FCSTD DOCUMENT  (FreeCAD 1.0R39109 (Git))
Label: Pistol
License: All rights reserved
LicenseURL: http://en.wikipedia.org/wiki/All_rights_reserved
objects: App::Link×6, Image::ImagePlane×1, App::Part×1
EXTERNAL_REF file=Parts/SizeRequirements.FCStd obj=Part
EXTERNAL_REF file=../../Reference/Pardini-SP22.FCStd obj=Part
EXTERNAL_REF file=Parts/Handgrip.stl.FCStd obj=Part
EXTERNAL_REF file=Parts/FrameAssembly.FCStd obj=Part
EXTERNAL_REF file=Parts/SidePlateRight.stl.FCStd obj=Part001
EXTERNAL_REF file=Parts/SidePlateLeft.stl.FCStd obj=Part

FEATURE [App::Link] Link  label="SizeRequirements"
  LinkPlacement = pos=(19.75,13.25,0) rot=(0,0,1;0rad)
  LinkedObject = -> <external Parts/SizeRequirements.FCStd>#Part
  Placement = pos=(19.75,13.25,0) rot=(0,0,1;0rad)
FEATURE [Image::ImagePlane] ecoaims_pp320expt  label="ecoaims-pp320expt"
  Placement = pos=(-5.6e-15,16,-29) rot=(0,-1,0;3.14159rad)
  XSize = 400.01
  YSize = 267.61
FEATURE [App::Link] Link003  label="Pardini-SP22"
  LinkPlacement = pos=(-49,5.84125e-06,-3.482e-13) rot=(0.57735,0.57735,0.57735;4.18879rad)
  LinkedObject = -> <external ../../Reference/Pardini-SP22.FCStd>#Part
  Placement = pos=(-49,5.84125e-06,-3.482e-13) rot=(0.57735,0.57735,0.57735;4.18879rad)
FEATURE [App::Link] Link008  label="Handgrip.stl"
  LinkPlacement = pos=(-80.0001,40,1.90735e-05) rot=(1,0,0;1.5708rad)
  LinkedObject = -> <external Parts/Handgrip.stl.FCStd>#Part
  Placement = pos=(-80.0001,40,1.90735e-05) rot=(1,0,0;1.5708rad)
FEATURE [App::Link] Link009  label="FrameAssembly"
  LinkedObject = -> <external Parts/FrameAssembly.FCStd>#Part
FEATURE [App::Link] Link010  label="SidePlateRight.stl"
  LinkPlacement = pos=(0,-1.07288e-06,9) rot=(0,0,1;0rad)
  LinkedObject = -> <external Parts/SidePlateRight.stl.FCStd>#Part001
  Placement = pos=(0,-1.07288e-06,9) rot=(0,0,1;0rad)
FEATURE [App::Link] Link011  label="SidePlateLeft.stl"
  LinkPlacement = pos=(-1.07288e-06,7.7486e-07,-9) rot=(1,0,0;3.14159rad)
  LinkedObject = -> <external Parts/SidePlateLeft.stl.FCStd>#Part
  Placement = pos=(-1.07288e-06,7.7486e-07,-9) rot=(1,0,0;3.14159rad)
FEATURE [App::Part] Part  label="Pistol"
  Group = -> [Link008,Link009,Link010,Link011]
  Origin = -> Origin

RESOLVED EXTERNAL PARTS (link-assembly join: the EXTERNAL_REF files above that resolve inside this repo's crawl, each included once):
---- part Parts/FrameAssembly.FCStd = doc fcstd_3d07353e2119 ----
FCSTD DOCUMENT  (FreeCAD 1.0R39109 (Git))
Label: FrameAssembly
License: All rights reserved
LicenseURL: http://en.wikipedia.org/wiki/All_rights_reserved
objects: App::Link×10, App::Part×1
EXTERNAL_REF file=FrameUpper.stl.FCStd obj=Part002
EXTERNAL_REF file=FrontSight.stl.FCStd obj=Part
EXTERNAL_REF file=../ReferenceParts/M3.FCStd obj=Part
EXTERNAL_REF file=RearSights/RearSightAssembly.FCStd obj=Part
EXTERNAL_REF file=TriggerPlate/TriggerPlateAssembly.FCStd obj=Part

FEATURE [App::Link] FrameUpperAssembly
  LinkedObject = -> <external FrameUpper.stl.FCStd>#Part002
FEATURE [App::Link] FrontSight_stl  label="FrontSight.stl"
  LinkPlacement = pos=(175,65,2.4354e-12) rot=(-1,0,0;1.5708rad)
  LinkedObject = -> <external FrontSight.stl.FCStd>#Part
  Placement = pos=(175,65,2.4354e-12) rot=(-1,0,0;1.5708rad)
FEATURE [App::Link] M3x022
  LinkPlacement = pos=(-95,62,5) rot=(1,0,0;4.71239rad)
  LinkedObject = -> <external ../ReferenceParts/M3.FCStd>#Part
  Placement = pos=(-95,62,5) rot=(1,0,0;4.71239rad)
FEATURE [App::Link] M3x023
  LinkPlacement = pos=(135,66.5,-5) rot=(-1,0,0;1.5708rad)
  LinkedObject = -> <external ../ReferenceParts/M3.FCStd>#Part
  Placement = pos=(135,66.5,-5) rot=(-1,0,0;1.5708rad)
FEATURE [App::Link] M3x025
  LinkPlacement = pos=(-55.1444,45.1136,-9) rot=(1,0,0;3.14159rad)
  LinkedObject = -> <external ../ReferenceParts/M3.FCStd>#Part
  Placement = pos=(-55.1444,45.1136,-9) rot=(1,0,0;3.14159rad)
FEATURE [App::Link] M3x026
  LinkPlacement = pos=(-130,62,-5) rot=(1,0,0;4.71239rad)
  LinkedObject = -> <external ../ReferenceParts/M3.FCStd>#Part
  Placement = pos=(-130,62,-5) rot=(1,0,0;4.71239rad)
FEATURE [App::Link] M3x027
  LinkPlacement = pos=(170,66.5,5) rot=(1,0,0;4.71239rad)
  LinkedObject = -> <external ../ReferenceParts/M3.FCStd>#Part
  Placement = pos=(170,66.5,5) rot=(1,0,0;4.71239rad)
FEATURE [App::Link] Link019  label="RearSightAssembly"
  LinkPlacement = pos=(-115,70,2.6148e-12) rot=(-1,0,0;1.5708rad)
  LinkedObject = -> <external RearSights/RearSightAssembly.FCStd>#Part
  Placement = pos=(-115,70,2.6148e-12) rot=(-1,0,0;1.5708rad)
FEATURE [App::Link] Link  label="TriggerPlateAssembly"
  LinkPlacement = pos=(-60,70,0) rot=(0,0,1;0rad)
  LinkedObject = -> <external TriggerPlate/TriggerPlateAssembly.FCStd>#Part
  Placement = pos=(-60,70,0) rot=(0,0,1;0rad)
FEATURE [App::Link] Link020  label="M3x028"
  LinkPlacement = pos=(4.75,45,-9) rot=(0,1,0;3.14159rad)
  LinkedObject = -> M3x025
  Placement = pos=(4.75,45,-9) rot=(0,1,0;3.14159rad)
FEATURE [App::Part] Part  label="FrameAssembly"
  Group = -> [Link,FrameUpperAssembly,FrontSight_stl,M3x022,M3x023,M3x025,M3x026,M3x027,Link019,Link020]
  Origin = -> Origin001
---- part Parts/Handgrip.stl.FCStd = doc fcstd_263e0108593d ----
FCSTD DOCUMENT  (FreeCAD 1.0R39109 (Git))
Label: Handgrip.stl
License: All rights reserved
LicenseURL: http://en.wikipedia.org/wiki/All_rights_reserved
objects: Sketcher::SketchObject×8, PartDesign::Pocket×5, PartDesign::Pad×2, PartDesign::Plane×2, PartDesign::Fillet×2, App::Link×1, PartDesign::Hole×1, PartDesign::Mirrored×1, PartDesign::Body×1, App::Part×1
note: 51 computed .brp shape members not serialized (recipe doc carries the construction recipe); baked Part::Feature solids carry a one-line shape summary decoded from their .brp
EXTERNAL_REF file=FrameUpper.stl.FCStd obj=Part

FEATURE [Sketcher::SketchObject] Sketch
  ArcFitTolerance = 1e-06
  AttachmentSupport = -> [XY_Plane]
  FullyConstrained = true
  MakeInternals = false
  MapMode = 5
  sketch-geometry (14):
    g0: LineSegment StartX=-47.9628 StartY=-46.6645 StartZ=0 EndX=-22.7127 EndY=-10.6036 EndZ=0
    g1: LineSegment StartX=-25.7393 StartY=9.8 StartZ=0 EndX=42 EndY=9.8 EndZ=0
    g2: LineSegment StartX=42 StartY=-18 StartZ=0 EndX=21 EndY=-18 EndZ=0
    g3: ArcOfCircle CenterX=26.2488 CenterY=-29.8933 CenterZ=0 NormalX=0 NormalY=0 NormalZ=1 AngleXU=0 Radius=13 StartAngle=1.98641 EndAngle=3.59864
    g4: ArcOfCircle CenterX=13.4151 CenterY=-65.1537 CenterZ=0 NormalX=0 NormalY=0 NormalZ=1 AngleXU=0 Radius=13 StartAngle=1.98641 EndAngle=3.59864
    g5: LineSegment StartX=-8.25041 StartY=-98.3649 StartZ=0 EndX=1.7494 EndY=-70.8906 EndZ=0
    g6: LineSegment [constr] StartX=13.4151 StartY=-65.1537 StartZ=0 EndX=26.2488 EndY=-29.8933 EndZ=0
    g7: LineSegment [constr] StartX=1.7494 StartY=-70.8906 StartZ=0 EndX=21 EndY=-18 EndZ=0
    g8: LineSegment StartX=42 StartY=9.8 StartZ=0 EndX=42 EndY=-18 EndZ=0
    g9: LineSegment StartX=-47.9628 StartY=-46.6645 StartZ=0 EndX=-59.9335 EndY=-79.5537 EndZ=0
    g10: LineSegment StartX=-59.9335 StartY=-79.5537 StartZ=0 EndX=-8.25041 EndY=-98.3649 EndZ=0
    g11: ArcOfCircle CenterX=-35 CenterY=-2 CenterZ=0 NormalX=0 NormalY=0 NormalZ=1 AngleXU=0 Radius=15 StartAngle=5.67232 EndAngle=7.18858
    g12: LineSegment [constr] StartX=26.2488 StartY=-29.8933 StartZ=0 EndX=14.0328 EndY=-25.447 EndZ=0
    g13: ArcOfCircle CenterX=19.8319 CenterY=-47.5235 CenterZ=0 NormalX=0 NormalY=0 NormalZ=1 AngleXU=0 Radius=13 StartAngle=1.98641 EndAngle=3.59864
  constraints (42):
    c: Horizontal(g1)
    c: DistanceY(g-1,g1) = 9.8
    c: Coincident(g3,g2)
    c: Coincident(g5,g4)
    c: Coincident(g6,g4)
    c: Coincident(g6,g3)
    c: Coincident(g7,g4)
    c: Coincident(g7,g2)
    c: PointOnObject(g3,g7)
    c: PointOnObject(g4,g7)
    c: Parallel(g7,g6)
    c: Radius(g3) = 13
    c: Coincident(g8,g1)
    c: Vertical(g8)
    c: Angle(g-1,g5) = 1.22173
    c: Parallel(g7,g5)
    c: Coincident(g9,g0)
    c: Parallel(g9,g5)
    c: Coincident(g10,g9)
    c: Coincident(g10,g5)
    c: Perpendicular(g9,g10)
    c: Distance(g9,g9) = 35
    c: Tangent(g0,g11) = -1.5708
    c: Radius(g11) = 15
    c: DistanceY(g11,g-1) = 2
    c: Angle(g-1,g0) = 0.959931
    c: Distance(g10,g10) = 55
    c: Coincident(g12,g3)
    c: PointOnObject(g12,g3)
    c: Perpendicular(g6,g12)
    c: Distance(g12,g7) = 4
    c: Coincident(g8,g2)
    c: Coincident(g1,g11)
    c: DistanceX(g11,g-1) = 35
    c: Symmetric(g6,g6,g13)
    c: Coincident(g13,g3)
    c: Coincident(g13,g4)
    c: Equal(g13,g3)
    c: DistanceX(g-1,g2) = 21
    c: DistanceY(g2,g-1) = 18
    c: Horizontal(g2)
    c: DistanceX(g-1,g2) = 42
FEATURE [App::Link] Link  label="FrameUpperReference"
  LinkPlacement = pos=(80,0,0) rot=(-1,0,0;1.5708rad)
  LinkedObject = -> <external FrameUpper.stl.FCStd>#Part
  Placement = pos=(80,0,0) rot=(-1,0,0;1.5708rad)
FEATURE [PartDesign::Pad] Pad
  Direction = (0,0,1)
  Length = 14
  Length2 = 22
  Midplane = true
  Profile = -> Sketch
  ReferenceAxis = -> Sketch [N_Axis]
  Refine = true
  Suppressed = false
  Type = 4
FEATURE [PartDesign::Plane] DatumPlane  label="HandgripTubeCutoutRef"
  AttachmentOffset = pos=(-17,0,50) rot=(0,-1,0;0.383972rad)
  AttachmentSupport = -> [XZ_Plane]
  Length = 156.334
  MapMode = 2
  Placement = pos=(-17,-50,1.11e-14) rot=(0.964231,-0.187428,-0.187428;1.60721rad)
  ResizeMode = 0
  Width = 66.7107
FEATURE [Sketcher::SketchObject] Sketch001
  ArcFitTolerance = 1e-06
  AttachmentSupport = -> [DatumPlane]
  FullyConstrained = true
  MakeInternals = false
  MapMode = 5
  Placement = pos=(-17,-50,1.11e-14) rot=(0.964231,-0.187428,-0.187428;1.60721rad)
  sketch-geometry (5):
    g0: ArcOfCircle CenterX=0 CenterY=0 CenterZ=0 NormalX=0 NormalY=0 NormalZ=1 AngleXU=0 Radius=15.25 StartAngle=2.48987 EndAngle=3.79332
    g1: ArcOfCircle CenterX=0 CenterY=0 CenterZ=0 NormalX=0 NormalY=0 NormalZ=1 AngleXU=0 Radius=15.25 StartAngle=5.63146 EndAngle=6.93491
    g2: LineSegment StartX=-12.1244 StartY=9.25 StartZ=0 EndX=12.1244 EndY=9.25 EndZ=0
    g3: LineSegment StartX=-12.1244 StartY=-9.25 StartZ=0 EndX=12.1244 EndY=-9.25 EndZ=0
    g4: Circle [constr] CenterX=0 CenterY=0 CenterZ=0 NormalX=0 NormalY=0 NormalZ=1 AngleXU=0 Radius=15.25
  constraints (15):
    c: Equal(g0,g1)
    c: Horizontal(g3)
    c: DistanceY(g1,g1) = 18.5
    c: Coincident(g2,g0)
    c: Coincident(g3,g0)
    c: Coincident(g3,g1)
    c: Coincident(g2,g1)
    c: PointOnObject(g4,g-2)
    c: Equal(g1,g4)
    c: Coincident(g1,g4)
    c: Horizontal(g2)
    c: Diameter(g4) = 30.5
    c: Coincident(g0,g1)
    c: Vertical(g0,g0)
    c: PointOnObject(g0,g-1)
FEATURE [Sketcher::SketchObject] Sketch003
  ArcFitTolerance = 1e-06
  AttachmentSupport = -> [YZ_Plane]
  FullyConstrained = true
  MakeInternals = false
  MapMode = 5
  Placement = pos=(0,0,0) rot=(0.57735,0.57735,0.57735;2.0944rad)
  sketch-geometry (7):
    g0: LineSegment StartX=-22.4833 StartY=-14 StartZ=0 EndX=-110 EndY=-14 EndZ=0
    g1: LineSegment StartX=-110 StartY=-14 StartZ=0 EndX=-110 EndY=-40 EndZ=0
    g2: LineSegment StartX=-110 StartY=-40 StartZ=0 EndX=0 EndY=-40 EndZ=0
    g3: LineSegment StartX=0 StartY=-40 StartZ=0 EndX=0 EndY=-27 EndZ=0
    g4: ArcOfCircle CenterX=-15 CenterY=-27 CenterZ=0 NormalX=0 NormalY=0 NormalZ=1 AngleXU=0 Radius=15 StartAngle=1e-16 EndAngle=2.09311
    g5: GeomPoint [constr] X=0 Y=-14 Z=0
    g6: GeomPoint X=-15 Y=-12 Z=0
  constraints (19):
    c: Coincident(g0,g1)
    c: Coincident(g1,g2)
    c: Coincident(g2,g3)
    c: Horizontal(g0)
    c: Horizontal(g2)
    c: Vertical(g1)
    c: Vertical(g3)
    c: DistanceY(g5,g-1) = 14
    c: DistanceX(g0,g-1) = 110
    c: PointOnObject(g5,g0)
    c: PointOnObject(g5,g3)
    c: Tangent(g3,g4) = -1.5708
    c: Radius(g4) = 15
    c: DistanceY(g2,g-1) = 40
    c: Coincident(g4,g0)
    c: DistanceY(g6,g-1) = 12
    c: PointOnObject(g6,g4)
    c: PointOnObject(g2,g-2)
    c: Vertical(g4,g6)
FEATURE [PartDesign::Pocket] Pocket002
  BaseFeature = -> Pad
  Direction = (-1,0,0)
  Length = 5
  Length2 = 5
  Midplane = true
  Profile = -> Sketch003
  ReferenceAxis = -> Sketch003 [N_Axis]
  Refine = true
  Suppressed = false
  Type = 1
FEATURE [PartDesign::Plane] DatumPlane001  label="HandgripFlatRef"
  AttachmentOffset = pos=(0,0,0) rot=(1,0,0;1.5708rad)
  AttachmentSupport = -> [DatumPlane]
  Length = 168.708
  MapMode = 5
  Placement = pos=(-17,-50,1.11e-14) rot=(0.981627,-0.190809,0;3.14159rad)
  ResizeMode = 0
  Width = 180.55
FEATURE [Sketcher::SketchObject] Sketch004
  ArcFitTolerance = 1e-06
  AttachmentOffset = pos=(0,0,25) rot=(0,0,1;0rad)
  AttachmentSupport = -> [DatumPlane001]
  FullyConstrained = true
  MakeInternals = false
  MapMode = 5
  Placement = pos=(-17,-50,-25) rot=(0.981627,-0.190809,0;3.14159rad)
  sketch-geometry (2):
    g0: Circle CenterX=0 CenterY=4 CenterZ=0 NormalX=0 NormalY=0 NormalZ=1 AngleXU=0 Radius=1.5
    g1: Circle CenterX=-15 CenterY=-56 CenterZ=0 NormalX=0 NormalY=0 NormalZ=1 AngleXU=0 Radius=1.5
  constraints (6):
    c: PointOnObject(g0,g-2)
    c: Equal(g1,g0)
    c: DistanceY(g-1,g0) = 4
    c: DistanceY(g1,g-1) = 56
    c: DistanceX(g1,g-1) = 15
    c: Diameter(g1) = 3
FEATURE [Sketcher::SketchObject] Sketch005
  ArcFitTolerance = 1e-06
  AttachmentOffset = pos=(0,0,-9.8) rot=(0,0,1;0rad)
  AttachmentSupport = -> [XZ_Plane]
  FullyConstrained = true
  MakeInternals = false
  MapMode = 5
  Placement = pos=(0,9.8,-2.2e-15) rot=(1,0,0;1.5708rad)
  sketch-geometry (4):
    g0: LineSegment StartX=-55 StartY=9 StartZ=0 EndX=-55 EndY=-9 EndZ=0
    g1: LineSegment StartX=-55 StartY=-9 StartZ=0 EndX=-20 EndY=-9 EndZ=0
    g2: LineSegment StartX=-20 StartY=-9 StartZ=0 EndX=-20 EndY=9 EndZ=0
    g3: LineSegment StartX=-20 StartY=9 StartZ=0 EndX=-55 EndY=9 EndZ=0
  constraints (11):
    c: Coincident(g0,g1)
    c: Coincident(g1,g2)
    c: Coincident(g2,g3)
    c: Coincident(g3,g0)
    c: Vertical(g2)
    c: Horizontal(g1)
    c: Horizontal(g3)
    c: DistanceX(g1,g-1) = 20
    c: DistanceX(g0,g-1) = 55
    c: DistanceY(g0,g0) = 18
    c: Symmetric(g0,g0,g-1)
FEATURE [Sketcher::SketchObject] Sketch006
  ArcFitTolerance = 1e-06
  AttachmentSupport = -> [DatumPlane001]
  FullyConstrained = true
  MakeInternals = false
  MapMode = 5
  Placement = pos=(-17,-50,1.11e-14) rot=(0.981627,-0.190809,0;3.14159rad)
  sketch-geometry (7):
    g0: LineSegment StartX=-66.2917 StartY=-80 StartZ=0 EndX=-10 EndY=-47.5 EndZ=0
    g1: LineSegment StartX=20 StartY=-54.5 StartZ=0 EndX=0 EndY=-54.5 EndZ=0
    g2: LineSegment StartX=-66.2917 StartY=-80 StartZ=0 EndX=80 EndY=-80 EndZ=0
    g3: LineSegment StartX=-10 StartY=-47.5 StartZ=0 EndX=0 EndY=-54.5 EndZ=0
    g4: LineSegment StartX=20 StartY=-54.5 StartZ=0 EndX=28.0805 EndY=-34.5 EndZ=0
    g5: LineSegment StartX=28.0805 StartY=-34.5 StartZ=0 EndX=80 EndY=-34.5 EndZ=0
    g6: LineSegment StartX=80 StartY=-34.5 StartZ=0 EndX=80 EndY=-80 EndZ=0
  constraints (21):
    c: Horizontal(g1)
    c: Distance(g0,g-2) = 10
    c: Angle(g-2,g0) = 2.0944
    c: Coincident(g2,g0)
    c: DistanceY(g0,g-1) = 47.5
    c: Coincident(g3,g0)
    c: Coincident(g3,g1)
    c: PointOnObject(g1,g-2)
    c: DistanceY(g1,g-1) = 54.5
    c: Distance(g1,g-2) = 20
    c: Horizontal(g2)
    c: DistanceY(g2,g-1) = 80
    c: Coincident(g4,g1)
    c: Coincident(g5,g4)
    c: Horizontal(g5)
    c: Coincident(g6,g5)
    c: Coincident(g6,g2)
    c: Vertical(g6)
    c: DistanceY(g1,g4) = 20
    c: DistanceX(g-1,g5) = 80
    c: Angle(g4,g-2) = 0.383972
FEATURE [Sketcher::SketchObject] Sketch007
  ArcFitTolerance = 1e-06
  AttachmentSupport = -> [XY_Plane]
  FullyConstrained = true
  MakeInternals = false
  MapMode = 5
  sketch-geometry (5):
    g0: Circle [constr] CenterX=25 CenterY=5 CenterZ=0 NormalX=0 NormalY=0 NormalZ=1 AngleXU=0 Radius=4
    g1: ArcOfCircle CenterX=25 CenterY=5 CenterZ=0 NormalX=0 NormalY=0 NormalZ=1 AngleXU=0 Radius=4 StartAngle=2.75762 EndAngle=5.89922
    g2: LineSegment StartX=28.7087 StartY=3.5016 StartZ=0 EndX=39.4148 EndY=30 EndZ=0
    g3: LineSegment StartX=21.2913 StartY=6.49843 StartZ=0 EndX=30.7865 EndY=30 EndZ=0
    g4: LineSegment StartX=30.7865 StartY=30 StartZ=0 EndX=39.4148 EndY=30 EndZ=0
  constraints (14):
    c: Diameter(g0) = 8
    c: Distance(g0,g-1) = 5
    c: DistanceX(g-1,g0) = 25
    c: Coincident(g1,g0)
    c: PointOnObject(g1,g0)
    c: Coincident(g2,g1)
    c: Tangent(g2,g0)
    c: Coincident(g4,g3)
    c: Coincident(g4,g2)
    c: Tangent(g3,g1) = 1.5708
    c: Horizontal(g4)
    c: DistanceY(g-1,g2) = 30
    c: Angle(g2,g-2) = 0.383972
    c: Parallel(g3,g2)
FEATURE [Sketcher::SketchObject] Sketch008
  ArcFitTolerance = 1e-06
  AttachmentSupport = -> [XZ_Plane]
  FullyConstrained = true
  MakeInternals = false
  MapMode = 5
  Placement = pos=(0,0,0) rot=(1,0,0;1.5708rad)
  sketch-geometry (4):
    g0: LineSegment StartX=80 StartY=0 StartZ=0 EndX=80 EndY=30 EndZ=0
    g1: LineSegment StartX=80 StartY=30 StartZ=0 EndX=25 EndY=30 EndZ=0
    g2: LineSegment StartX=25 StartY=30 StartZ=0 EndX=25 EndY=0 EndZ=0
    g3: LineSegment StartX=25 StartY=0 StartZ=0 EndX=80 EndY=0 EndZ=0
  constraints (12):
    c: Coincident(g0,g1)
    c: Coincident(g1,g2)
    c: Coincident(g2,g3)
    c: Coincident(g3,g0)
    c: Vertical(g0)
    c: Vertical(g2)
    c: Horizontal(g1)
    c: Horizontal(g3)
    c: PointOnObject(g0,g-1)
    c: DistanceX(g-1,g1) = 25
    c: DistanceX(g-1,g0) = 80
    c: DistanceY(g0,g0) = 30
FEATURE [PartDesign::Pocket] Pocket005
  BaseFeature = -> Pocket002
  Direction = (0,1,-2e-16)
  Length = 5
  Length2 = 5
  Midplane = true
  Profile = -> Sketch008
  ReferenceAxis = -> Sketch008 [N_Axis]
  Refine = true
  Suppressed = false
  Type = 1
FEATURE [PartDesign::Fillet] Fillet
  Base = -> Pocket005 [Edge19,Edge18,Edge20,Edge21,Edge6,Edge5,Edge25,Edge34,Edge7,Edge22,Edge8,Edge3,Edge14,Edge15,Edge30,Edge23,Edge10,Edge1,Edge31]
  BaseFeature = -> Pocket005
  Radius = 12.5
  Refine = true
  SupportTransform = false
  Suppressed = false
  UseAllEdges = false
FEATURE [PartDesign::Fillet] Fillet001
  Base = -> Fillet [Face2,Edge27,Edge50,Edge58,Edge79,Edge83,Edge78,Edge56,Edge69]
  BaseFeature = -> Fillet
  Radius = 3
  Refine = true
  SupportTransform = false
  Suppressed = false
  UseAllEdges = false
FEATURE [PartDesign::Hole] Hole  label="FastningBoltHoles"
  BaseFeature = -> Fillet001
  CustomThreadClearance = 0
  Depth = 30
  DepthType = 0
  Diameter = 3.4
  DrillForDepth = false
  DrillPoint = 1
  DrillPointAngle = 118
  HoleCutCountersinkAngle = 90
  HoleCutCustomValues = false
  HoleCutDepth = 14
  HoleCutDiameter = 8
  HoleCutType = 1
  ModelThread = false
  Profile = -> Sketch004
  Refine = true
  Suppressed = false
  Tapered = false
  TaperedAngle = 90
  ThreadClass = 0
  ThreadDepth = 30
  ThreadDepthType = 0
  ThreadDirection = 0
  ThreadFit = 0
  ThreadSize = 9
  ThreadType = 1
  Threaded = false
  UseCustomThreadClearance = false
FEATURE [PartDesign::Mirrored] Mirrored
  BaseFeature = -> Hole
  MirrorPlane = -> XY_Plane
  Originals = -> [Hole]
  Refine = true
  Suppressed = false
  TransformMode = 0
FEATURE [PartDesign::Pocket] Pocket  label="BatteryTubeCutout"
  BaseFeature = -> Mirrored
  Direction = (0.374607,0.927184,-1e-16)
  Length = 100
  Length2 = 12
  Profile = -> Sketch001
  ReferenceAxis = -> Sketch001 [N_Axis]
  Refine = true
  Suppressed = false
  Type = 4
FEATURE [PartDesign::Pocket] Pocket003  label="FrameCutout"
  BaseFeature = -> Pocket
  Direction = (0,0,1)
  Length = 18.5
  Length2 = 5
  Midplane = true
  Profile = -> Sketch006
  ReferenceAxis = -> Sketch006 [N_Axis]
  Refine = true
  Suppressed = false
  Type = 0
FEATURE [PartDesign::Pad] Pad001  label="RearSupportPad"
  BaseFeature = -> Pocket003
  Direction = (0,-1,2e-16)
  Length = 2
  Length2 = 10
  Profile = -> Sketch005
  ReferenceAxis = -> Sketch005 [N_Axis]
  Refine = true
  Suppressed = false
  Type = 0
FEATURE [PartDesign::Pocket] Pocket004  label="TriggerPlateScrewCutout"
  BaseFeature = -> Pad001
  Direction = (0,0,-1)
  Length = 5
  Length2 = 5
  Profile = -> Sketch007
  ReferenceAxis = -> Sketch007 [N_Axis]
  Refine = true
  Suppressed = false
  Type = 1
FEATURE [PartDesign::Body] Body
  AllowCompound = false
  Group = -> [Sketch,Pad,DatumPlane,Sketch001,Sketch003,Pocket002,Sketch008,Pocket005,Fillet,DatumPlane001,Sketch004,Fillet001,Hole,Mirrored,Pocket,Sketch005,Sketch006,Pocket003,Pad001,Sketch007,Pocket004]
  Origin = -> Origin
  Placement = pos=(0,0,0) rot=(1,0,0;4.71239rad)
  Tip = -> Pocket005
FEATURE [App::Part] Part  label="Handgrip.stl"
  Group = -> [Body]
  Origin = -> Origin001
---- part Parts/SidePlateLeft.stl.FCStd = doc fcstd_c89c702df72f ----
FCSTD DOCUMENT  (FreeCAD 1.0R39109 (Git))
Label: SidePlateLeft.stl
License: All rights reserved
LicenseURL: http://en.wikipedia.org/wiki/All_rights_reserved
objects: App::Link×1, Part::Mirroring×1, PartDesign::FeatureBase×1, Sketcher::SketchObject×1, PartDesign::Pocket×1, PartDesign::Body×1, App::Part×1
note: 9 computed .brp shape members not serialized (recipe doc carries the construction recipe); baked Part::Feature solids carry a one-line shape summary decoded from their .brp
EXTERNAL_REF file=SidePlateRight.stl.FCStd obj=Body

FEATURE [App::Link] Link  label="SidePlateRight"
  LinkedObject = -> <external SidePlateRight.stl.FCStd>#Body
FEATURE [Part::Mirroring] Part__Mirroring  label="SidePlateLeft"
  Base = (0,0,0)
  Normal = (0,1,0)
  Source = -> Link
FEATURE [PartDesign::FeatureBase] BaseFeature
  BaseFeature = -> Part__Mirroring
  Suppressed = false
FEATURE [Sketcher::SketchObject] Sketch
  ArcFitTolerance = 1e-06
  AttachmentSupport = -> [XY_Plane001]
  FullyConstrained = true
  MakeInternals = false
  MapMode = 5
  sketch-geometry (1):
    g0: Circle CenterX=4.75 CenterY=-45 CenterZ=0 NormalX=0 NormalY=0 NormalZ=1 AngleXU=0 Radius=3.5
  constraints (3):
    c: Diameter(g0) = 7
    c: DistanceY(g0,g-1) = 45
    c: Distance(g0,g-2) = 4.75
FEATURE [PartDesign::Pocket] Pocket
  BaseFeature = -> BaseFeature
  Direction = (0,0,-1)
  Length = 5
  Length2 = 5
  Midplane = true
  Profile = -> Sketch
  ReferenceAxis = -> Sketch [N_Axis]
  Refine = true
  Suppressed = false
  Type = 1
FEATURE [PartDesign::Body] Body
  AllowCompound = false
  BaseFeature = -> Part__Mirroring
  Group = -> [BaseFeature,Sketch,Pocket]
  Origin = -> Origin001
  Tip = -> Pocket
FEATURE [App::Part] Part  label="SidePlateLeft.stl"
  Group = -> [Link,Part__Mirroring,Body]
  Origin = -> Origin
---- part Parts/SidePlateRight.stl.FCStd = doc fcstd_58ffd16d6dbb ----
FCSTD DOCUMENT  (FreeCAD 1.0R39109 (Git))
Label: SidePlateRight.stl
License: All rights reserved
LicenseURL: http://en.wikipedia.org/wiki/All_rights_reserved
objects: Sketcher::SketchObject×2, PartDesign::Pad×1, PartDesign::Chamfer×1, PartDesign::Hole×1, PartDesign::Body×1, App::Part×1
note: 14 computed .brp shape members not serialized (recipe doc carries the construction recipe); baked Part::Feature solids carry a one-line shape summary decoded from their .brp

FEATURE [Sketcher::SketchObject] Sketch
  ArcFitTolerance = 1e-06
  AttachmentSupport = -> [XY_Plane002]
  FullyConstrained = true
  MakeInternals = false
  MapMode = 5
  sketch-geometry (14):
    g0: LineSegment StartX=-135 StartY=62 StartZ=0 EndX=-135 EndY=50 EndZ=0
    g1: LineSegment StartX=-135 StartY=50 StartZ=0 EndX=-20 EndY=50 EndZ=0
    g2: LineSegment StartX=-20 StartY=50 StartZ=0 EndX=-5 EndY=35 EndZ=0
    g3: LineSegment StartX=10 StartY=14 StartZ=0 EndX=160 EndY=14 EndZ=0
    g4: LineSegment StartX=160 StartY=14 StartZ=0 EndX=175 EndY=29 EndZ=0
    g5: LineSegment StartX=175 StartY=29 StartZ=0 EndX=175 EndY=70 EndZ=0
    g6: LineSegment StartX=-85 StartY=70 StartZ=0 EndX=-135 EndY=62 EndZ=0
    g7: LineSegment StartX=-85 StartY=70 StartZ=0 EndX=-26 EndY=70 EndZ=0
    g8: LineSegment StartX=-26 StartY=70 StartZ=0 EndX=-18 EndY=62 EndZ=0
    g9: LineSegment StartX=-18 StartY=62 StartZ=0 EndX=10 EndY=62 EndZ=0
    g10: LineSegment StartX=10 StartY=62 StartZ=0 EndX=10 EndY=70 EndZ=0
    g11: LineSegment StartX=175 StartY=70 StartZ=0 EndX=10 EndY=70 EndZ=0
    g12: LineSegment StartX=-5 StartY=35 StartZ=0 EndX=10 EndY=35 EndZ=0
    g13: LineSegment StartX=10 StartY=35 StartZ=0 EndX=10 EndY=14 EndZ=0
  constraints (42):
    c: Vertical(g0)
    c: Coincident(g0,g1)
    c: Horizontal(g1)
    c: Coincident(g1,g2)
    c: Horizontal(g3)
    c: Coincident(g3,g4)
    c: Coincident(g4,g5)
    c: Vertical(g5)
    c: Coincident(g6,g0)
    c: DistanceX(g0,g-1) = 135
    c: DistanceY(g0,g0) = 12
    c: DistanceY(g-1,g0) = 50
    c: DistanceX(g-1,g3) = 10
    c: DistanceY(g-1,g2) = 35
    c: DistanceY(g-1,g3) = 14
    c: DistanceX(g-1,g4) = 175
    c: DistanceX(g3,g4) = 15
    c: Angle(g3,g4) = 0.785398
    c: DistanceY(g-1,g5) = 70
    c: DistanceX(g0,g6) = 50
    c: Coincident(g7,g6)
    c: Horizontal(g7)
    c: Coincident(g8,g7)
    c: Coincident(g9,g8)
    c: Horizontal(g9)
    c: Coincident(g11,g5)
    c: Coincident(g11,g10)
    c: Horizontal(g11)
    c: Vertical(g10)
    c: DistanceX(g-1,g10) = 10
    c: Coincident(g9,g10)
    c: DistanceY(g10,g10) = 8
    c: Horizontal(g7,g10)
    c: DistanceX(g8,g-1) = 18
    c: Angle(g9,g8) = 2.35619
    c: Angle(g2,g1) = 0.785398
    c: Coincident(g12,g2)
    c: Horizontal(g12)
    c: Coincident(g13,g12)
    c: Coincident(g13,g3)
    c: Vertical(g13)
    c: DistanceX(g12,g12) = 15
FEATURE [PartDesign::Pad] Pad
  Direction = (0,0,1)
  Length = 4
  Length2 = 10
  Profile = -> Sketch
  ReferenceAxis = -> Sketch [N_Axis]
  Refine = true
  Suppressed = false
  Type = 0
FEATURE [PartDesign::Chamfer] Chamfer
  Angle = 45
  Base = -> Pad [Face16]
  BaseFeature = -> Pad
  ChamferType = 0
  FlipDirection = false
  Refine = true
  Size = 1.5
  Size2 = 1
  SupportTransform = false
  Suppressed = false
  UseAllEdges = false
FEATURE [Sketcher::SketchObject] Sketch001
  ArcFitTolerance = 1e-06
  AttachmentOffset = pos=(0,0,10) rot=(0,0,1;0rad)
  AttachmentSupport = -> [XY_Plane002]
  FullyConstrained = true
  MakeInternals = false
  MapMode = 5
  Placement = pos=(0,0,10) rot=(0,0,1;0rad)
  sketch-geometry (5):
    g0: Circle CenterX=-125 CenterY=55 CenterZ=0 NormalX=0 NormalY=0 NormalZ=1 AngleXU=0 Radius=1.5
    g1: Circle CenterX=-65 CenterY=65 CenterZ=0 NormalX=0 NormalY=0 NormalZ=1 AngleXU=0 Radius=1.5
    g2: Circle CenterX=16 CenterY=35 CenterZ=0 NormalX=0 NormalY=0 NormalZ=1 AngleXU=0 Radius=1.5
    g3: Circle CenterX=125 CenterY=65 CenterZ=0 NormalX=0 NormalY=0 NormalZ=1 AngleXU=0 Radius=1.5
    g4: Circle CenterX=170 CenterY=35 CenterZ=0 NormalX=0 NormalY=0 NormalZ=1 AngleXU=0 Radius=1.5
  constraints (15):
    c: DistanceX(g-1,g4) = 170
    c: DistanceY(g-1,g4) = 35
    c: DistanceY(g-1,g3) = 65
    c: DistanceX(g-1,g3) = 125
    c: DistanceX(g-1,g2) = 16
    c: DistanceY(g-1,g2) = 35
    c: DistanceX(g1,g-1) = 65
    c: DistanceY(g-1,g1) = 65
    c: DistanceX(g0,g-1) = 125
    c: DistanceY(g-1,g0) = 55
    c: Equal(g0,g1)
    c: Equal(g1,g2)
    c: Equal(g2,g4)
    c: Equal(g4,g3)
    c: Diameter(g4) = 3
FEATURE [PartDesign::Hole] Hole
  BaseFeature = -> Chamfer
  CustomThreadClearance = 0
  Depth = 25
  DepthType = 0
  Diameter = 3.4
  DrillForDepth = false
  DrillPoint = 1
  DrillPointAngle = 118
  HoleCutCountersinkAngle = 90
  HoleCutCustomValues = false
  HoleCutDepth = 7.5
  HoleCutDiameter = 6.1
  HoleCutType = 1
  ModelThread = false
  Profile = -> Sketch001
  Refine = true
  Suppressed = false
  Tapered = false
  TaperedAngle = 90
  ThreadClass = 0
  ThreadDepth = 25
  ThreadDepthType = 0
  ThreadDirection = 0
  ThreadFit = 0
  ThreadSize = 9
  ThreadType = 1
  Threaded = false
  UseCustomThreadClearance = false
FEATURE [PartDesign::Body] Body  label="SidePlateRight"
  AllowCompound = false
  Group = -> [Sketch,Pad,Chamfer,Sketch001,Hole]
  Origin = -> Origin002
  Tip = -> Hole
FEATURE [App::Part] Part001  label="SidePlateRight.stl"
  Group = -> [Body]
  Origin = -> Origin001
  Placement = pos=(0,0,9) rot=(0,0,1;0rad)
---- part Parts/SizeRequirements.FCStd = doc fcstd_d00a57abd4df ----
FCSTD DOCUMENT  (FreeCAD 1.0R39109 (Git))
Label: SizeRequirements
License: All rights reserved
LicenseURL: http://en.wikipedia.org/wiki/All_rights_reserved
objects: Sketcher::SketchObject×2, PartDesign::Pad×2, PartDesign::Body×2, App::Part×1
note: 12 computed .brp shape members not serialized (recipe doc carries the construction recipe); baked Part::Feature solids carry a one-line shape summary decoded from their .brp

FEATURE [Sketcher::SketchObject] Sketch
  ArcFitTolerance = 1e-06
  AttachmentSupport = -> [XY_Plane]
  FullyConstrained = true
  MakeInternals = false
  MapMode = 5
  sketch-geometry (4):
    g0: LineSegment StartX=-210 StartY=100 StartZ=0 EndX=-210 EndY=-100 EndZ=0
    g1: LineSegment StartX=-210 StartY=-100 StartZ=0 EndX=210 EndY=-100 EndZ=0
    g2: LineSegment StartX=210 StartY=-100 StartZ=0 EndX=210 EndY=100 EndZ=0
    g3: LineSegment StartX=210 StartY=100 StartZ=0 EndX=-210 EndY=100 EndZ=0
  constraints (11):
    c: Coincident(g0,g1)
    c: Coincident(g1,g2)
    c: Coincident(g2,g3)
    c: Coincident(g3,g0)
    c: Vertical(g0)
    c: Vertical(g2)
    c: Horizontal(g1)
    c: Horizontal(g3)
    c: Symmetric(g1,g0,g-1)
    c: DistanceX(g3,g3) = 420
    c: Distance(g0,g0) = 200
FEATURE [PartDesign::Pad] Pad
  Direction = (0,0,1)
  Length = 50
  Length2 = 10
  Midplane = true
  Profile = -> Sketch
  ReferenceAxis = -> Sketch [N_Axis]
  Refine = true
  Suppressed = false
  Type = 0
FEATURE [PartDesign::Body] Body  label="Size Requirement Max"
  AllowCompound = false
  Group = -> [Sketch,Pad]
  Origin = -> Origin
  Tip = -> Pad
FEATURE [Sketcher::SketchObject] Sketch001
  ArcFitTolerance = 1e-06
  AttachmentSupport = -> [XY_Plane001]
  FullyConstrained = true
  MakeInternals = false
  MapMode = 5
  sketch-geometry (4):
    g0: LineSegment StartX=-168 StartY=-80 StartZ=0 EndX=168 EndY=-80 EndZ=0
    g1: LineSegment StartX=168 StartY=-80 StartZ=0 EndX=168 EndY=80 EndZ=0
    g2: LineSegment StartX=168 StartY=80 StartZ=0 EndX=-168 EndY=80 EndZ=0
    g3: LineSegment StartX=-168 StartY=80 StartZ=0 EndX=-168 EndY=-80 EndZ=0
  constraints (11):
    c: Coincident(g0,g1)
    c: Coincident(g1,g2)
    c: Coincident(g2,g3)
    c: Coincident(g3,g0)
    c: Horizontal(g0)
    c: Horizontal(g2)
    c: Vertical(g1)
    c: Vertical(g3)
    c: Symmetric(g0,g2,g-1)
    c: DistanceX(g0,g0) = 336
    c: DistanceY(g1,g1) = 160
FEATURE [PartDesign::Pad] Pad001
  Direction = (0,0,1)
  Length = 40
  Length2 = 10
  Midplane = true
  Profile = -> Sketch001
  ReferenceAxis = -> Sketch001 [N_Axis]
  Refine = true
  Suppressed = false
  Type = 0
FEATURE [PartDesign::Body] Body001  label="Size Requirement Min"
  AllowCompound = false
  Group = -> [Sketch001,Pad001]
  Origin = -> Origin001
  Tip = -> Pad001
FEATURE [App::Part] Part  label="SizeRequirements"
  Group = -> [Body001,Body]
  Origin = -> Origin002
